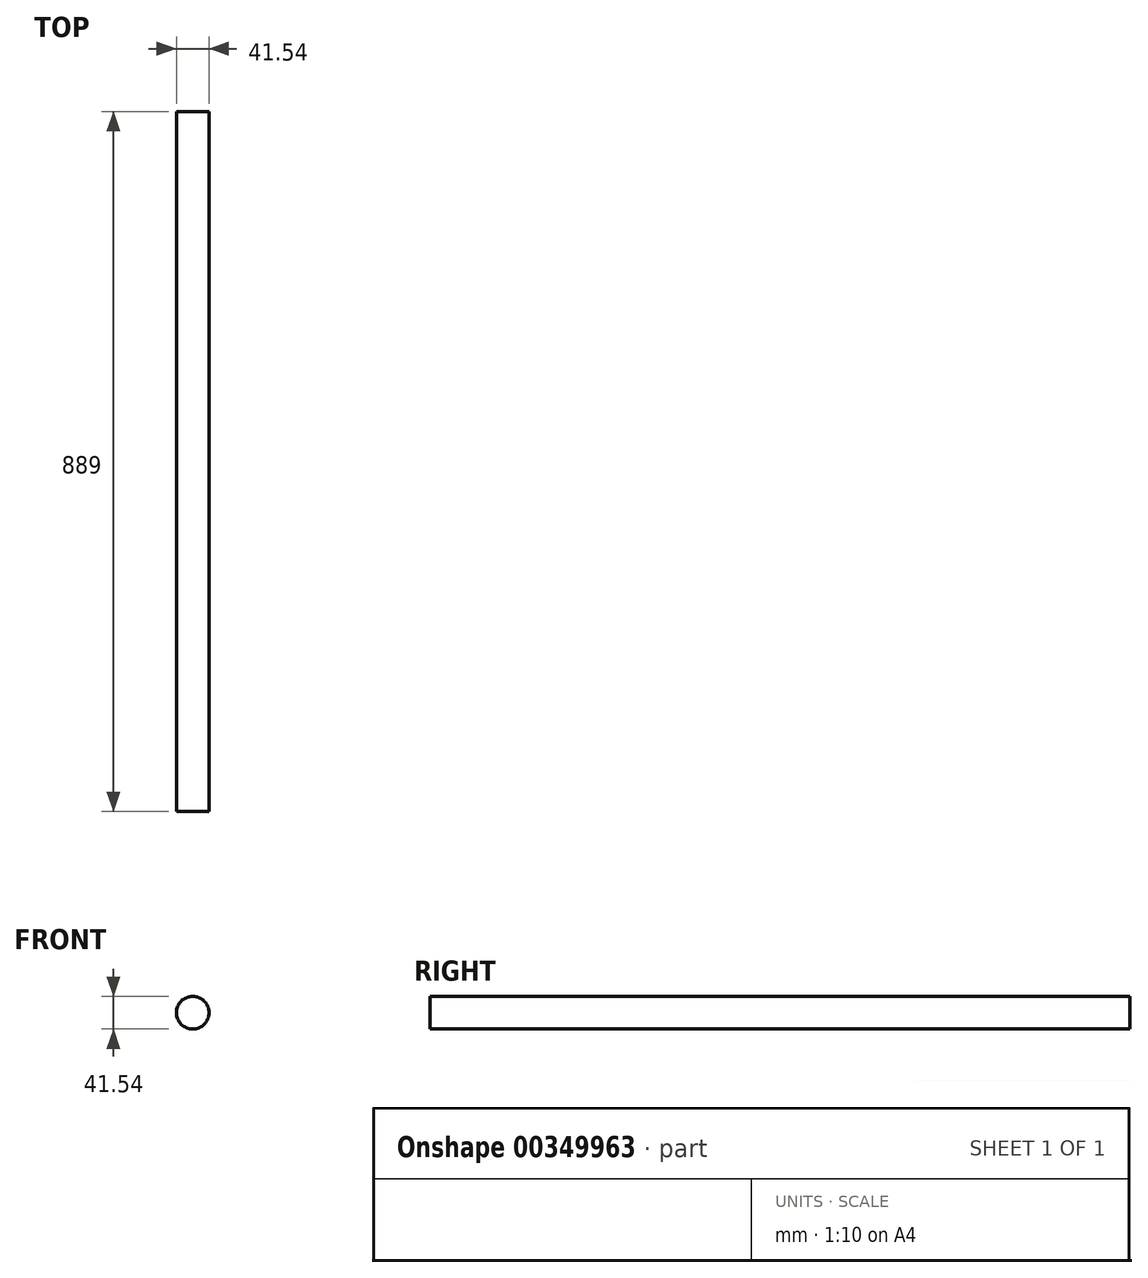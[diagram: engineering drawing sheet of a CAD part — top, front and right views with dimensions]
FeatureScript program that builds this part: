
annotation { "Feature Type Name" : "Feature", "Feature Type Description" : "" }
export const myFeature = defineFeature(function(context is Context, id is Id, definition is map)
    precondition{}
    {
        {
            var Q0;
            Q0=qCreatedBy(makeId("Front.planeOp"),FACE);
            var sketch = newSketch(context, id + "F0", { "sketchPlane" : qUnion([Q0])});
            skCircle(sketch, "E0", {"center": v(0, 0) * mm, "radius": 20.77 * mm});
            skSolve(sketch);
        }
        {
            var Q0;
            Q0 = qSketchRegion(id + "F0", true);
            extrude(context, id + "F1", {"entities" : qUnion([Q0]), "depth" : 889 * mm});
        }
    });
